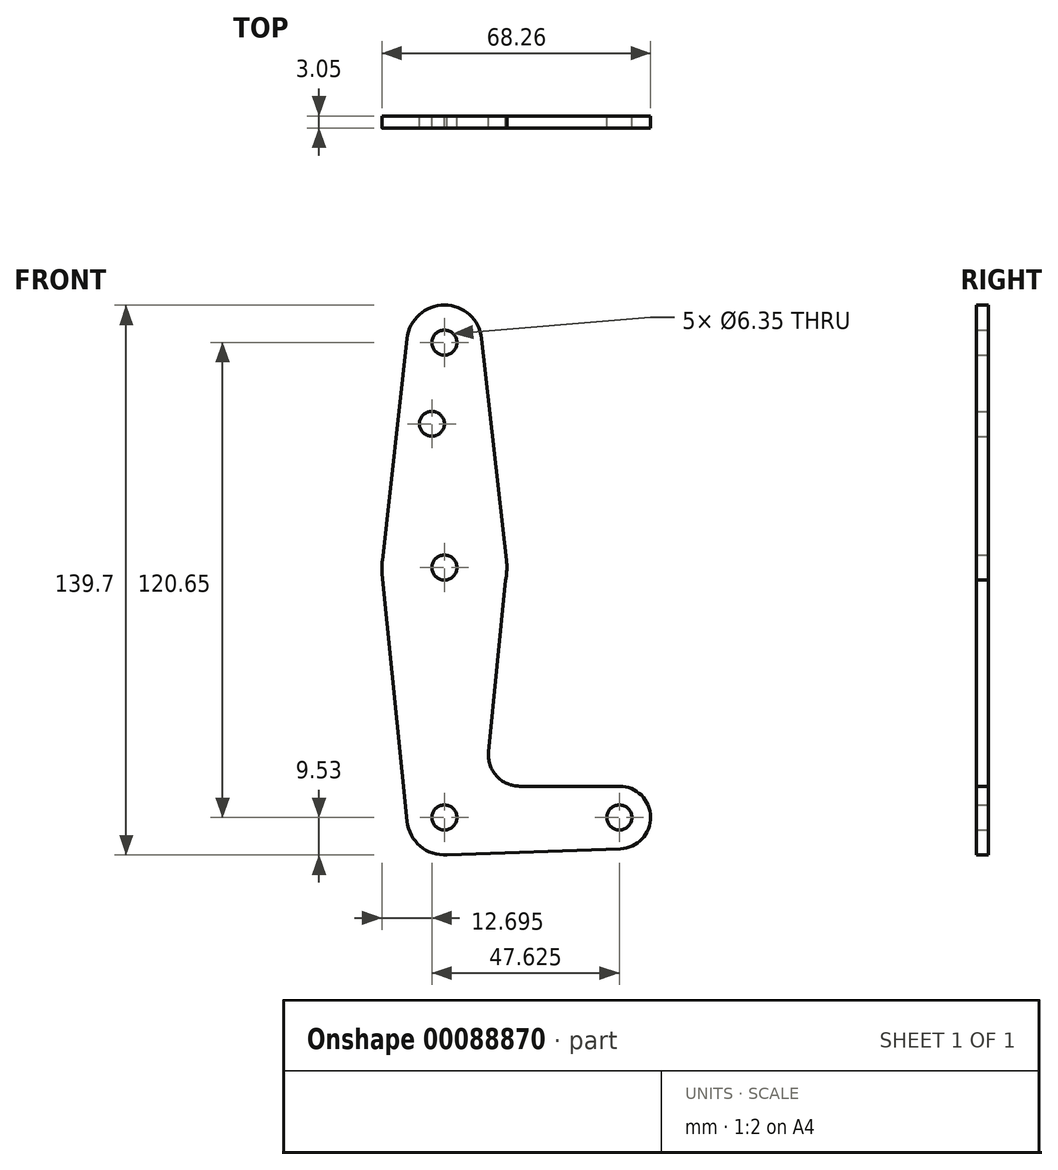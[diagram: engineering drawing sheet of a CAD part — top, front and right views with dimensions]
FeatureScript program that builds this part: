
annotation { "Feature Type Name" : "Feature", "Feature Type Description" : "" }
export const myFeature = defineFeature(function(context is Context, id is Id, definition is map)
    precondition{}
    {
        {
            var Q0;
            Q0=qCreatedBy(makeId("Front.planeOp"),FACE);
            var sketch = newSketch(context, id + "F0", { "sketchPlane" : qUnion([Q0])});
            skLineSegment(sketch, "E0", {"start": v(0, 0) * mm, "end": v(0, 120.65) * mm, "construction": true});
            skLineSegment(sketch, "E1", {"start": v(0, 0) * mm, "end": v(44.45, 0) * mm, "construction": true});
            skCircle(sketch, "E2", {"center": v(0, 0) * mm, "radius": 9.53 * mm});
            skCircle(sketch, "E3", {"center": v(44.45, 0) * mm, "radius": 7.94 * mm});
            skCircle(sketch, "E4", {"center": v(0, 120.65) * mm, "radius": 9.53 * mm});
            skCircle(sketch, "E5", {"center": v(0, 120.65) * mm, "radius": 3.18 * mm});
            skCircle(sketch, "E6", {"center": v(0, 63.5) * mm, "radius": 15.88 * mm});
            skLineSegment(sketch, "E7", {"start": v(19.14, 7.94) * mm, "end": v(44.45, 7.94) * mm});
            skLineSegment(sketch, "E8", {"start": v(0, -9.52) * mm, "end": v(44.73, -7.93) * mm});
            skLineSegment(sketch, "E9", {"start": v(-9.47, 121.7) * mm, "end": v(-15.78, 65.26) * mm});
            skLineSegment(sketch, "E10", {"start": v(9.47, 121.7) * mm, "end": v(15.78, 65.26) * mm});
            skLineSegment(sketch, "E11", {"start": v(15.88, 63.5) * mm, "end": v(11.23, 16.67) * mm});
            skCircle(sketch, "E12", {"center": v(0, 63.5) * mm, "radius": 3.18 * mm});
            skCircle(sketch, "E13", {"center": v(0, 0) * mm, "radius": 3.18 * mm});
            skCircle(sketch, "E14", {"center": v(44.45, 0) * mm, "radius": 3.18 * mm});
            skArc(sketch, "E15.filletArc", {"start": v(11.23, 16.67) * mm, "mid": v(13.25, 10.55) * mm, "end": v(19.14, 7.94) * mm});
            skCircle(sketch, "E16", {"center": v(-3.17, 100.03) * mm, "radius": 3.18 * mm});
            skLineSegment(sketch, "E17", {"start": v(-15.8, 61.91) * mm, "end": v(-9.48, -0.95) * mm});
            skSolve(sketch);
        }
        {
            var Q0;
            Q0 = qSketchRegion(id + "F0", true);
            extrude(context, id + "F1", {"entities" : qUnion([Q0]), "depth" : 3.05 * mm});
        }
    });
